# Revit family: Midmark Central Scavenger
name_source: partatom
category: Specialty Equipment
revit_build: Autodesk Revit 2017 (Build: 20190507_1515(x64)
units: mm (PartAtom-declared; Revit-internal decimal feet)

## family parameters
Always vertical = Yes
Cut with Voids When Loaded = No
Part Type = Normal
Room Calculation Point = No
Round Connector Dimension = Use Diameter
Shared = No
Work Plane-Based = No

## types (2) — shared parameters
Cut Sheet #1 = <None>
Cut Sheet #2 = <None>
Cut Sheet #3 = <None>
Depth = 0' - 8 21/32"
Frame Material = Steel, Paint Finish, Midmark - Pebble Grey
Height = 1' - 2 3/16"
Manufacturer = Midmark
Midmark Graphics = Yes
Width = 1' - 1 17/32"

## per-type parameters (varying)
| type | Description | Model |
| Central Scavenger | For Up to Four Anesthesia Machines | 40162800 |
| Central Scavenger with Expansion Kit | For Up to Four Anesthesia Machines. Expansion Kit Allows for Up to Four Additional Anesthesia Machines | 40162800 & 20236000 |

note: column(s) folded — value = type name in every type: Type Comments

## geometry (parser evidence)
native form markers: Sweep x3
no freeform markers — native parametric forms only
